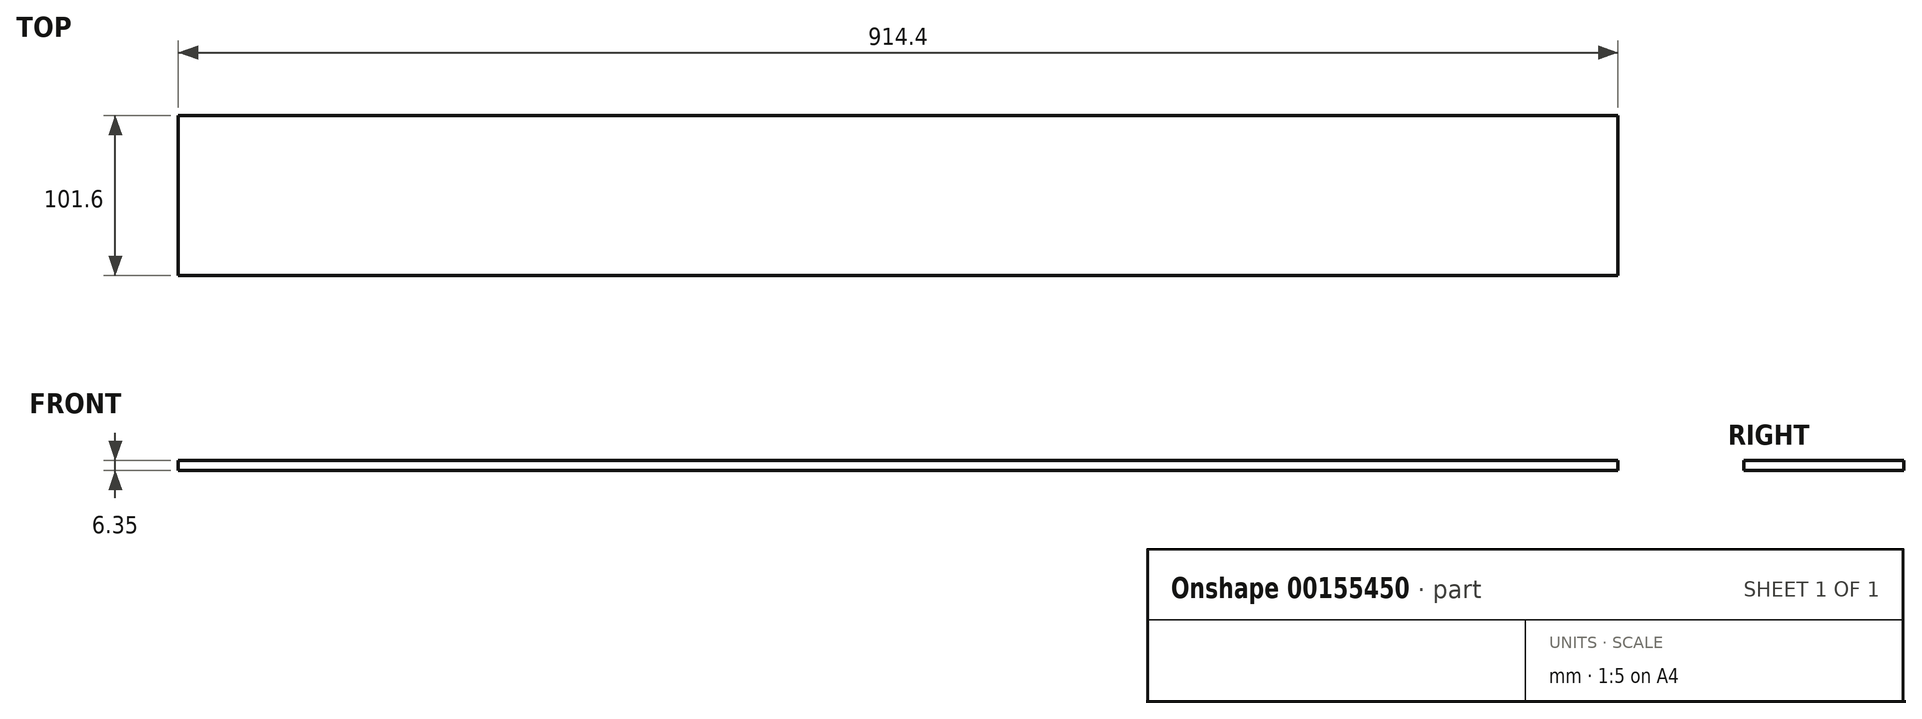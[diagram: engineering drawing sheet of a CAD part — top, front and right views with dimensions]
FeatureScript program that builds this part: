
annotation { "Feature Type Name" : "Feature", "Feature Type Description" : "" }
export const myFeature = defineFeature(function(context is Context, id is Id, definition is map)
    precondition{}
    {
        {
            var Q0;
            Q0=qCreatedBy(makeId("Top.planeOp"),FACE);
            var sketch = newSketch(context, id + "F0", { "sketchPlane" : qUnion([Q0])});
            skLineSegment(sketch, "E0.bottom", {"start": v(0, 0) * mm, "end": v(914.4, 0) * mm});
            skLineSegment(sketch, "E0.top", {"start": v(0, 101.6) * mm, "end": v(914.4, 101.6) * mm});
            skLineSegment(sketch, "E0.left", {"start": v(0, 0) * mm, "end": v(0, 101.6) * mm});
            skLineSegment(sketch, "E0.right", {"start": v(914.4, 0) * mm, "end": v(914.4, 101.6) * mm});
            skSolve(sketch);
        }
        {
            var Q0;
            Q0 = qSketchRegion(id + "F0", true);
            extrude(context, id + "F1", {"entities" : qUnion([Q0]), "depth" : 6.35 * mm});
        }
    });
